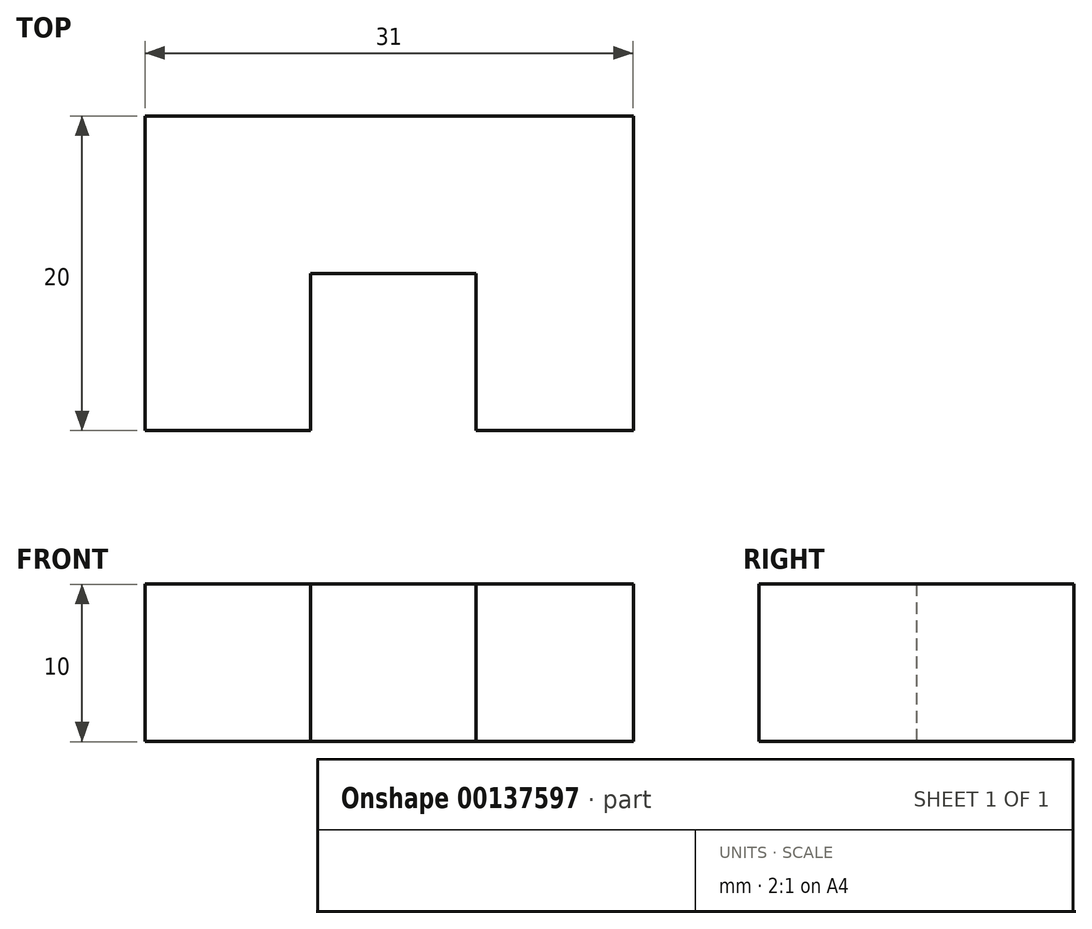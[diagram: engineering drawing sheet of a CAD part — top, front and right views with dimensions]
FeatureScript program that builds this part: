
annotation { "Feature Type Name" : "Feature", "Feature Type Description" : "" }
export const myFeature = defineFeature(function(context is Context, id is Id, definition is map)
    precondition{}
    {
        {
            var Q0;
            Q0=qCreatedBy(makeId("Front.planeOp"),FACE);
            var sketch = newSketch(context, id + "F0", { "sketchPlane" : qUnion([Q0])});
            skLineSegment(sketch, "E0", {"start": v(-29.4, 0.87) * mm, "end": v(1.6, 0.87) * mm});
            skLineSegment(sketch, "E1", {"start": v(1.6, 0.87) * mm, "end": v(1.6, 10.87) * mm});
            skLineSegment(sketch, "E2", {"start": v(1.6, 10.87) * mm, "end": v(-29.4, 10.87) * mm});
            skLineSegment(sketch, "E3", {"start": v(-29.4, 0.87) * mm, "end": v(-29.4, 10.87) * mm});
            skLineSegment(sketch, "E4", {"start": v(-19.4, 10.87) * mm, "end": v(-19.4, 0.87) * mm});
            skLineSegment(sketch, "E5", {"start": v(-8.4, 0.87) * mm, "end": v(-8.4, 10.87) * mm});
            skSolve(sketch);
        }
        {
            var Q0;
            {var subQ0=sQuery(id+"F0.wireOp",EDGE,"E3");Q0=makeQuery(id+"F0.imprint","IMPRINT",FACE,{"disambiguationData":[TD([[makeQuery(id+"F0.imprint","IMPRINT",EDGE,{"derivedFrom":subQ0}),-1.0]])]});}
            var Q1;
            {var subQ0=sQuery(id+"F0.wireOp",EDGE,"E4");Q1=makeQuery(id+"F0.imprint","IMPRINT",FACE,{"disambiguationData":[TD([[makeQuery(id+"F0.imprint","IMPRINT",EDGE,{"derivedFrom":subQ0}),1.0]])]});}
            extrude(context, id + "F1", {"entities" : qUnion([Q0, Q1]), "depth" : 20 * mm});
        }
        {
            var Q0;
            Q0=makeQuery(id+"F1.opExtrude","CAP_FACE",FACE,{"disambiguationData":[OSD([sQuery(id+"F0.wireOp",EDGE,"E0"),sQuery(id+"F0.wireOp",EDGE,"E2"),sQuery(id+"F0.wireOp",EDGE,"E3"),sQuery(id+"F0.wireOp",EDGE,"E5")])],"isStart":false});
            var sketch = newSketch(context, id + "F2", { "sketchPlane" : qUnion([Q0])});
            skLineSegment(sketch, "E6.bottom", {"start": v(-8.4, 10.87) * mm, "end": v(-18.9, 10.87) * mm});
            skLineSegment(sketch, "E6.top", {"start": v(-8.4, 0.87) * mm, "end": v(-18.9, 0.87) * mm});
            skLineSegment(sketch, "E6.left", {"start": v(-8.4, 10.87) * mm, "end": v(-8.4, 0.87) * mm});
            skLineSegment(sketch, "E6.right", {"start": v(-18.9, 10.87) * mm, "end": v(-18.9, 0.87) * mm});
            skSolve(sketch);
        }
        {
            var Q0;
            Q0=makeQuery(id+"F2.imprint","IMPRINT",FACE,{"disambiguationData":[TD([[makeQuery(id+"F2.imprint","IMPRINT",EDGE,{"derivedFrom":sQuery(id+"F2.wireOp",EDGE,"E6.bottom")}),1.0]])]});
            extrude(context, id + "F3", {"entities" : qUnion([Q0]), "operationType" : NewBodyOperationType.REMOVE, "oppositeDirection" : true, "depth" : 10 * mm});
        }
        {
            var Q0;
            {var subQ0=sQuery(id+"F0.wireOp",EDGE,"E1");Q0=makeQuery(id+"F0.imprint","IMPRINT",FACE,{"disambiguationData":[TD([[makeQuery(id+"F0.imprint","IMPRINT",EDGE,{"derivedFrom":subQ0}),1.0]])]});}
            extrude(context, id + "F4", {"entities" : qUnion([Q0]), "operationType" : NewBodyOperationType.ADD, "depth" : 20 * mm});
        }
    });
